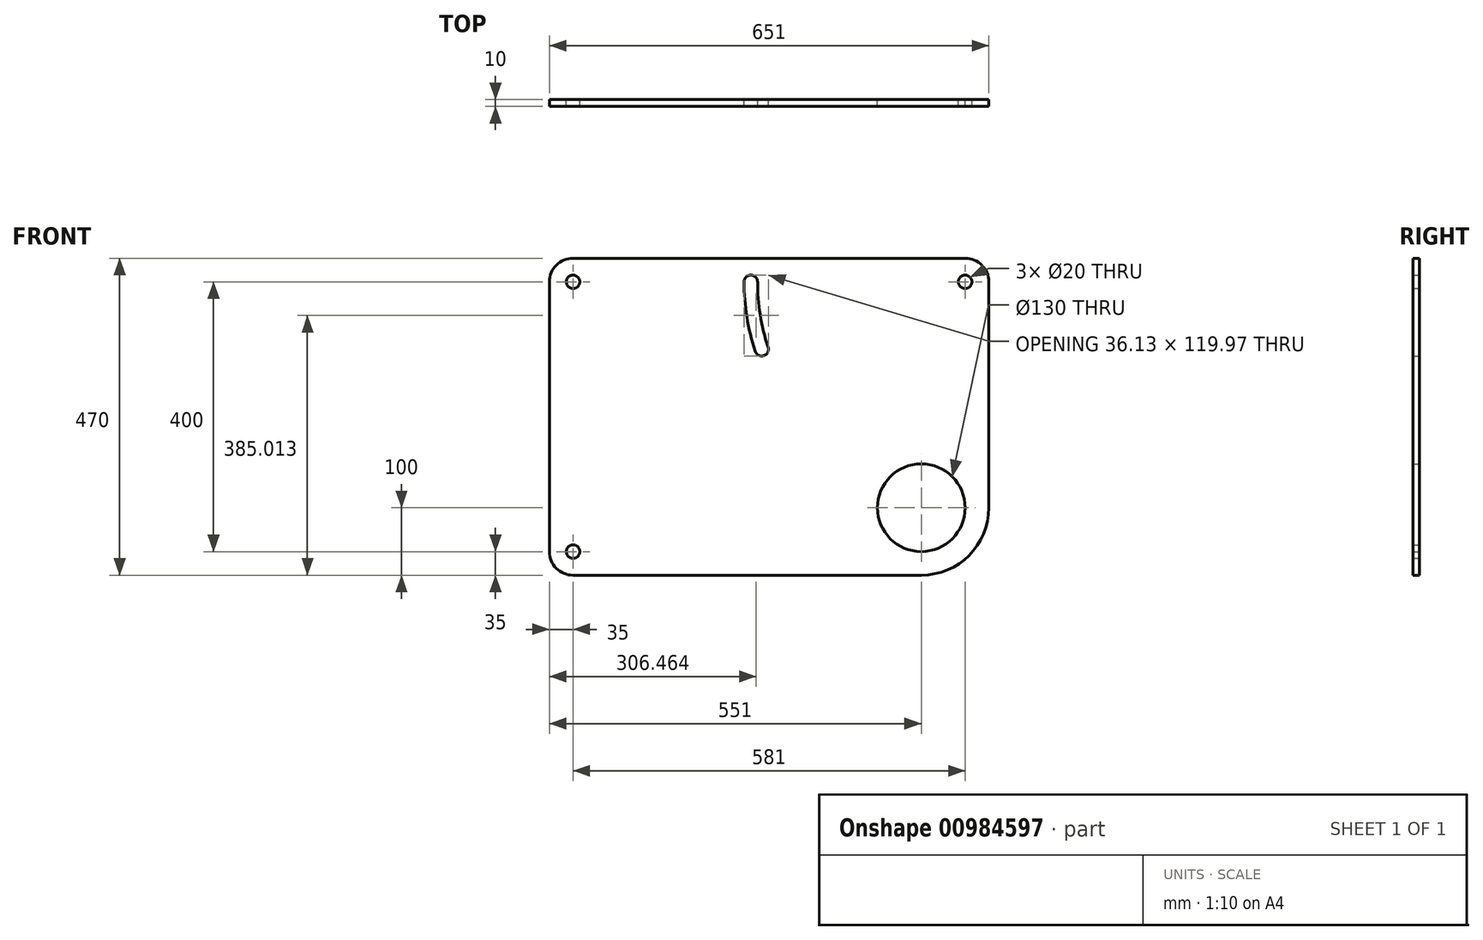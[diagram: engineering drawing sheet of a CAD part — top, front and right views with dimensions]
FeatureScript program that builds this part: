
annotation { "Feature Type Name" : "Feature", "Feature Type Description" : "" }
export const myFeature = defineFeature(function(context is Context, id is Id, definition is map)
    precondition{}
    {
        {
            var Q0;
            Q0=qCreatedBy(makeId("Front.planeOp"),FACE);
            var sketch = newSketch(context, id + "F0", { "sketchPlane" : qUnion([Q0])});
            skArc(sketch, "E0", {"start": v(-35, 0) * mm, "mid": v(-24.75, -24.75) * mm, "end": v(0, -35) * mm});
            skArc(sketch, "E1", {"start": v(516, -35) * mm, "mid": v(586.71, -5.71) * mm, "end": v(616, 65) * mm});
            skArc(sketch, "E2", {"start": v(0, 435) * mm, "mid": v(-24.75, 424.75) * mm, "end": v(-35, 400) * mm});
            skCircle(sketch, "E3", {"center": v(263.4, 400) * mm, "radius": 35 * mm, "construction": true});
            skLineSegment(sketch, "E4", {"start": v(0, -35) * mm, "end": v(516, -35) * mm});
            skLineSegment(sketch, "E5", {"start": v(-35, 400) * mm, "end": v(-35, 0) * mm});
            skLineSegment(sketch, "E6", {"start": v(0, 435) * mm, "end": v(263.4, 435) * mm});
            skArc(sketch, "E7", {"start": v(616, 400) * mm, "mid": v(605.75, 424.75) * mm, "end": v(581, 435) * mm});
            skLineSegment(sketch, "E8", {"start": v(616, 400) * mm, "end": v(616, 65) * mm});
            skLineSegment(sketch, "E9", {"start": v(263.4, 435) * mm, "end": v(581, 435) * mm});
            skCircle(sketch, "E10", {"center": v(581, 400) * mm, "radius": 10 * mm});
            skCircle(sketch, "E11", {"center": v(516, 65) * mm, "radius": 65 * mm});
            skCircle(sketch, "E12", {"center": v(0, 0) * mm, "radius": 10 * mm});
            skCircle(sketch, "E13", {"center": v(0, 400) * mm, "radius": 10 * mm});
            skArc(sketch, "E14", {"start": v(263.4, 400) * mm, "mid": v(267.46, 349.35) * mm, "end": v(279.55, 300) * mm, "construction": true});
            skArc(sketch, "E15.0.startCap", {"start": v(253.4, 400) * mm, "mid": v(263.4, 410) * mm, "end": v(273.4, 400) * mm});
            skArc(sketch, "E15.0.endCap", {"start": v(289.05, 303.15) * mm, "mid": v(282.7, 290.5) * mm, "end": v(270.06, 296.85) * mm});
            skArc(sketch, "E15.0.left", {"start": v(273.4, 400) * mm, "mid": v(277.34, 350.95) * mm, "end": v(289.05, 303.15) * mm});
            skArc(sketch, "E15.0.right", {"start": v(253.4, 400) * mm, "mid": v(257.6, 347.76) * mm, "end": v(270.06, 296.85) * mm});
            skCircle(sketch, "E16", {"center": v(0, 400) * mm, "radius": 35 * mm, "construction": true});
            skCircle(sketch, "E17", {"center": v(581, 400) * mm, "radius": 35 * mm, "construction": true});
            skCircle(sketch, "E18", {"center": v(516, 65) * mm, "radius": 100 * mm, "construction": true});
            skCircle(sketch, "E19", {"center": v(0, 0) * mm, "radius": 35 * mm, "construction": true});
            skSolve(sketch);
        }
        {
            var Q0;
            Q0=makeQuery(id+"F0.imprint","IMPRINT",FACE,{"disambiguationData":[TD([[makeQuery(id+"F0.imprint","IMPRINT",EDGE,{"derivedFrom":sQuery(id+"F0.wireOp",EDGE,"E0")}),1.0]])]});
            extrude(context, id + "F1", {"entities" : qUnion([Q0]), "depth" : 10 * mm, "offsetDistance" : 25.4 * mm});
        }
    });
